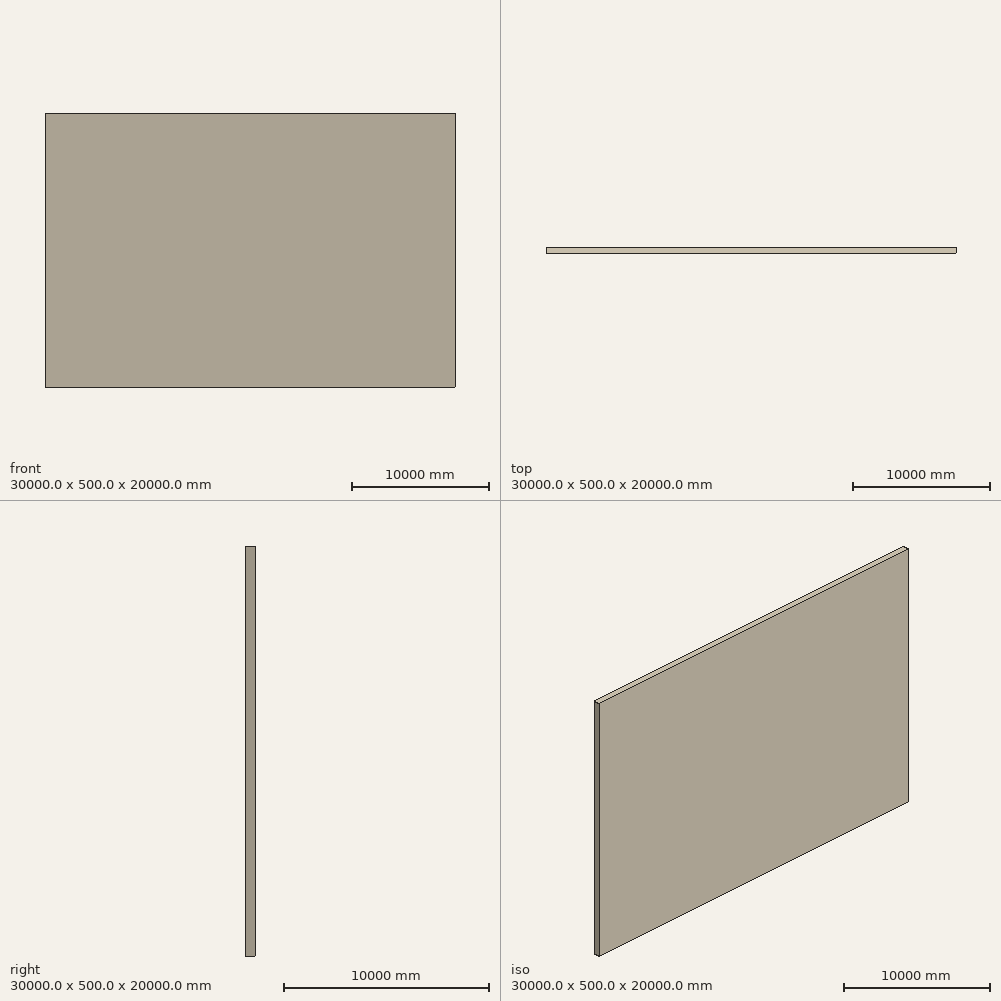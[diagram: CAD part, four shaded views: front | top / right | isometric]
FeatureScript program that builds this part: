
annotation { "Feature Type Name" : "Feature", "Feature Type Description" : "" }
export const myFeature = defineFeature(function(context is Context, id is Id, definition is map)
    precondition{}
    {
        {
            var Q0;
            Q0=qCreatedBy(makeId("Top.planeOp"),FACE);
            var sketch = newSketch(context, id + "F0", { "sketchPlane" : qUnion([Q0])});
            skLineSegment(sketch, "E0.bottom", {"start": v(-30000, 500) * mm, "end": v(0, 500) * mm});
            skLineSegment(sketch, "E0.top", {"start": v(-30000, 0) * mm, "end": v(0, 0) * mm});
            skLineSegment(sketch, "E0.left", {"start": v(-30000, 500) * mm, "end": v(-30000, 0) * mm});
            skLineSegment(sketch, "E0.right", {"start": v(0, 500) * mm, "end": v(0, 0) * mm});
            skSolve(sketch);
        }
        {
            var Q0;
            Q0 = qSketchRegion(id + "F0", true);
            extrude(context, id + "F1", {"entities" : qUnion([Q0]), "depth" : 20000 * mm});
        }
    });
